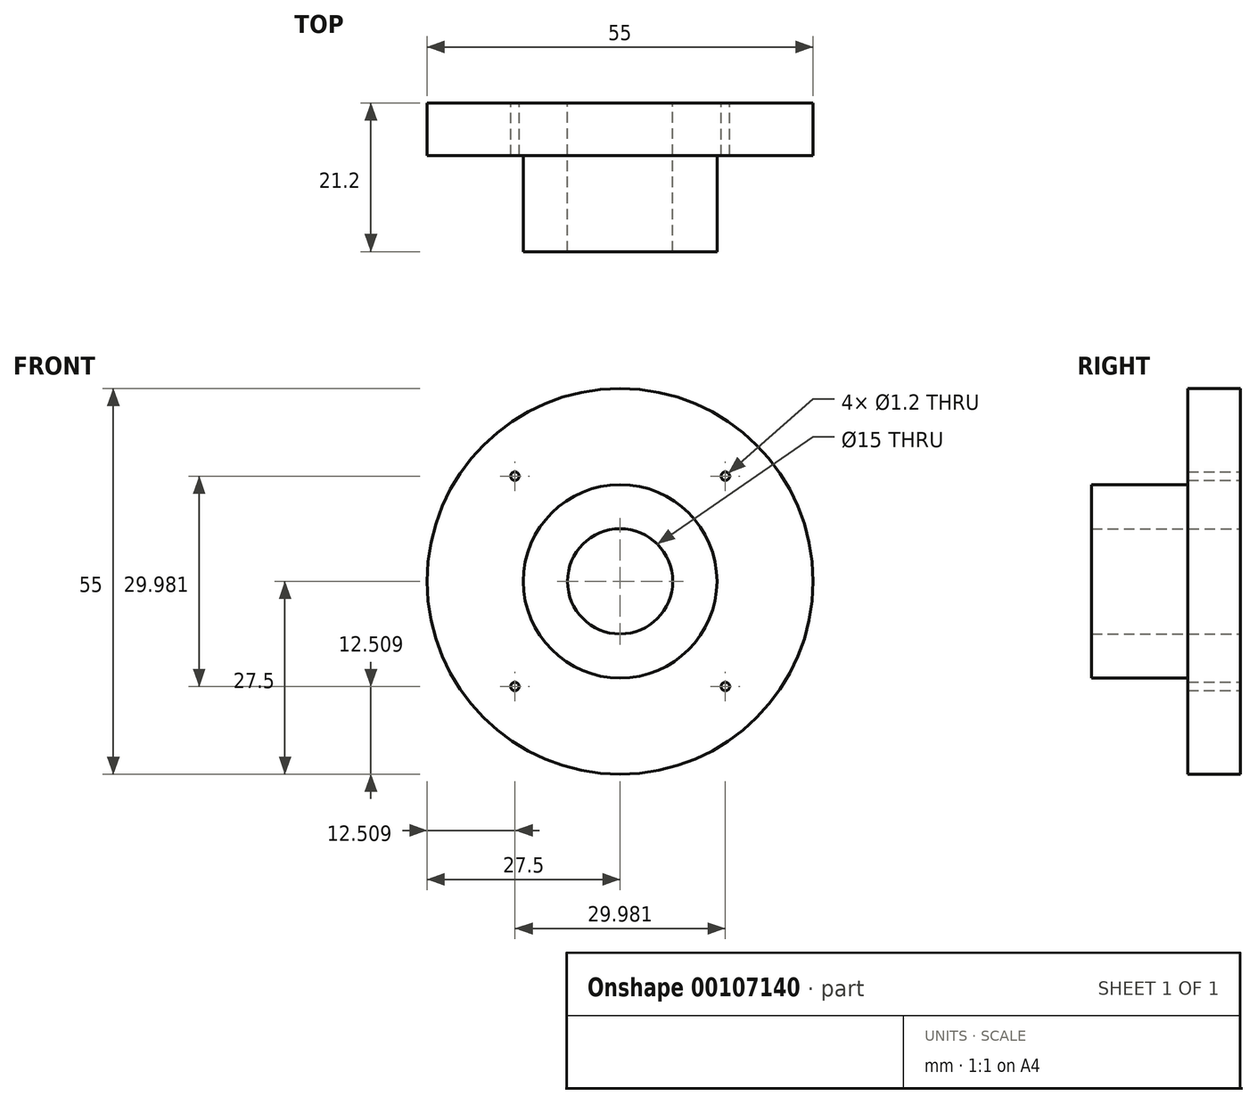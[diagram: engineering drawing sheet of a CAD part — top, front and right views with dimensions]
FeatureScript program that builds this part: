
annotation { "Feature Type Name" : "Feature", "Feature Type Description" : "" }
export const myFeature = defineFeature(function(context is Context, id is Id, definition is map)
    precondition{}
    {
        {
            var Q0;
            Q0=qCreatedBy(makeId("Front.planeOp"),FACE);
            var sketch = newSketch(context, id + "F0", { "sketchPlane" : qUnion([Q0])});
            skCircle(sketch, "E0", {"center": v(0, 0) * mm, "radius": 27.5 * mm});
            skCircle(sketch, "E1", {"center": v(0, 0) * mm, "radius": 13.8 * mm});
            skCircle(sketch, "E2", {"center": v(0, 0) * mm, "radius": 7.5 * mm});
            skCircle(sketch, "E3", {"center": v(0, 0) * mm, "radius": 21.2 * mm, "construction": true});
            skLineSegment(sketch, "E4", {"start": v(0, 0) * mm, "end": v(-31.33, 31.33) * mm, "construction": true});
            skCircle(sketch, "E5", {"center": v(-15, 15) * mm, "radius": 0.6 * mm});
            skCircle(sketch, "E6.MirrorC", {"center": v(15, 15) * mm, "radius": 0.6 * mm});
            skCircle(sketch, "E7.MirrorC", {"center": v(-15, -15) * mm, "radius": 0.6 * mm});
            skCircle(sketch, "E8.MirrorC", {"center": v(15, -15) * mm, "radius": 0.6 * mm});
            skSolve(sketch);
        }
        {
            var Q0;
            Q0=makeQuery(id+"F0.imprint","IMPRINT",FACE,{"disambiguationData":[TD([[makeQuery(id+"F0.imprint","IMPRINT",EDGE,{"derivedFrom":sQuery(id+"F0.wireOp",EDGE,"E0")}),1.0]])]});
            extrude(context, id + "F1", {"entities" : qUnion([Q0]), "depth" : 7.5 * mm});
        }
        {
            var Q0;
            Q0=makeQuery(id+"F0.imprint","IMPRINT",FACE,{"disambiguationData":[TD([[makeQuery(id+"F0.imprint","IMPRINT",EDGE,{"derivedFrom":sQuery(id+"F0.wireOp",EDGE,"E1")}),1.0]])]});
            extrude(context, id + "F2", {"entities" : qUnion([Q0]), "operationType" : NewBodyOperationType.ADD, "depth" : 21.2 * mm});
        }
    });
